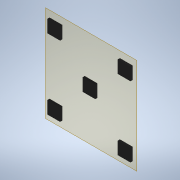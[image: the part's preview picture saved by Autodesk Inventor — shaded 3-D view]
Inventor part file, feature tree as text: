
AUTODESK INVENTOR PART (.ipt)
format: ipt  version: 2020 (Build 240168000, 168)  size: 126,976 bytes
history: native  units: in
note: dims shown in document units (in); Inventor stores cm internally (conversion verified against a paired STEP export)
features: other x3, plane x1, extrude x1, sketch x1
ambient origin geometry x8: Origin, YZ Plane, XZ Plane, XY Plane, X Axis, Y Axis, Z Axis, Center Point
bodies: Solid1 (feature_tree)
feature tree (6):
  plane  "Work Plane1"
  extrude  "Extrusion1"  Depth=6.0in
  sketch  "Sketch1"  dims[d0=6.0in d1=6.0in d2=39.3701in d3=39.3701in d4=0.7874in d6=33.3701in d7=0.7874in d9=33.3701in d12=6.0in d13=6.0in d14=1.0in d15=0.0in]
  other  "<userpath>\Documents\inventor\md\Project\Assembly2.iam"
  other  "Assembly2.iam"
  other  "Part6:1"
